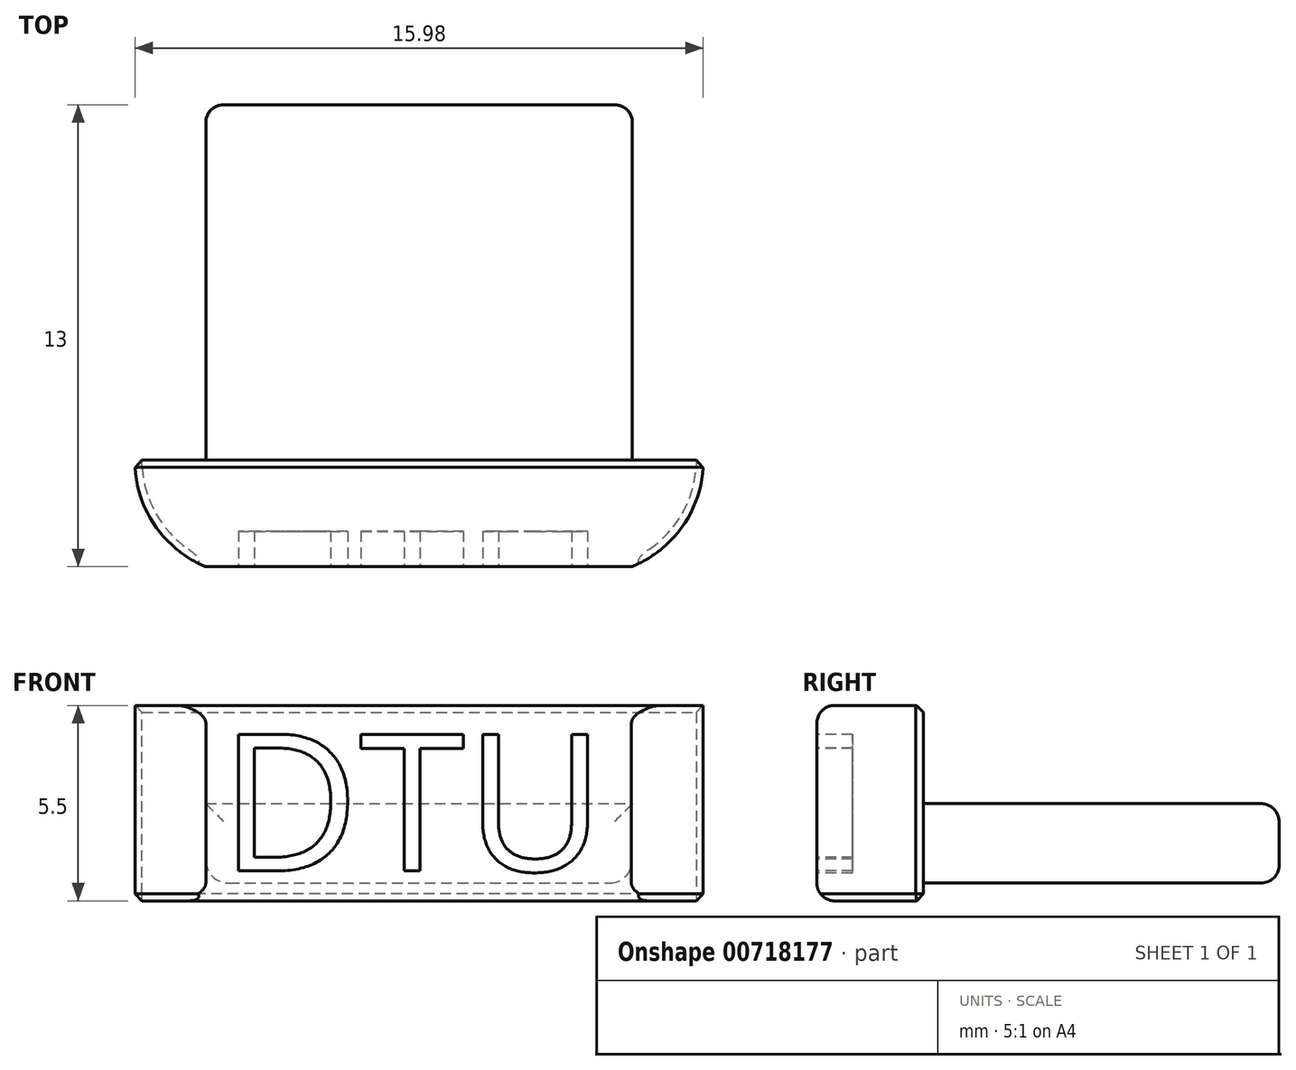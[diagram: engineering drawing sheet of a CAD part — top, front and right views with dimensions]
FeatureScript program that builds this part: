
annotation { "Feature Type Name" : "Feature", "Feature Type Description" : "" }
export const myFeature = defineFeature(function(context is Context, id is Id, definition is map)
    precondition{}
    {
        {
            var Q0;
            Q0=qCreatedBy(makeId("Front.planeOp"),FACE);
            var sketch = newSketch(context, id + "F0", { "sketchPlane" : qUnion([Q0])});
            skLineSegment(sketch, "E0.bottom", {"start": v(0.64, 0) * mm, "end": v(11.36, 0) * mm});
            skLineSegment(sketch, "E1.top", {"start": v(0.31, 2.24) * mm, "end": v(11.69, 2.24) * mm});
            skPoint(sketch, "E2.visualSharp", {"position": v(12, 4.5) * mm});
            skPoint(sketch, "E3.visualSharp", {"position": v(0, 4.5) * mm});
            skPoint(sketch, "E4.visualSharp", {"position": v(0, 0) * mm});
            skArc(sketch, "E4.filletArc", {"start": v(0, 0.64) * mm, "mid": v(0.19, 0.19) * mm, "end": v(0.64, 0) * mm});
            skPoint(sketch, "E5.visualSharp", {"position": v(12, 0) * mm});
            skArc(sketch, "E5.filletArc", {"start": v(11.36, 0) * mm, "mid": v(11.81, 0.19) * mm, "end": v(12, 0.64) * mm});
            skPoint(sketch, "E6.visualSharp", {"position": v(0.31, 4.18) * mm});
            skPoint(sketch, "E7.visualSharp", {"position": v(11.69, 4.18) * mm});
            skPoint(sketch, "E8.visualSharp", {"position": v(0.32, 0.31) * mm});
            skPoint(sketch, "E9.visualSharp", {"position": v(11.69, 0.32) * mm});
            skLineSegment(sketch, "E10", {"start": v(0.31, 2.24) * mm, "end": v(0, 2.24) * mm});
            skLineSegment(sketch, "E11", {"start": v(11.69, 2.24) * mm, "end": v(12, 2.24) * mm});
            skLineSegment(sketch, "E12", {"start": v(12, 0.64) * mm, "end": v(12, 2.24) * mm});
            skLineSegment(sketch, "E13", {"start": v(0, 0.64) * mm, "end": v(0, 2.24) * mm});
            skSolve(sketch);
        }
        {
            var Q0;
            Q0=makeQuery(id+"F0.imprint","IMPRINT",FACE,{"disambiguationData":[TD([[makeQuery(id+"F0.imprint","IMPRINT",EDGE,{"derivedFrom":sQuery(id+"F0.wireOp",EDGE,"E0.bottom")}),1.0]])]});
            var Q1;
            Q1=makeQuery(id+"F0.imprint","IMPRINT",FACE,{"disambiguationData":[TD([[makeQuery(id+"F0.imprint","IMPRINT",EDGE,{"derivedFrom":sQuery(id+"F0.wireOp",EDGE,"E1.bottom")}),-1.0]])]});
            extrude(context, id + "F1", {"entities" : qUnion([Q0, Q1]), "depth" : 10 * mm, "offsetDistance" : 25 * mm});
        }
        {
            var Q0;
            Q0=makeQuery(id+"F1.opExtrude","CAP_FACE",FACE,{"disambiguationData":[OSD([sQuery(id+"F0.wireOp",EDGE,"E0.bottom"),sQuery(id+"F0.wireOp",EDGE,"E0.top"),sQuery(id+"F0.wireOp",EDGE,"E0.left"),sQuery(id+"F0.wireOp",EDGE,"E0.right"),sQuery(id+"F0.wireOp",EDGE,"E2.filletArc"),sQuery(id+"F0.wireOp",EDGE,"E3.filletArc"),sQuery(id+"F0.wireOp",EDGE,"E4.filletArc"),sQuery(id+"F0.wireOp",EDGE,"E5.filletArc")])],"isStart":false});
            var sketch = newSketch(context, id + "F2", { "sketchPlane" : qUnion([Q0])});
            skLineSegment(sketch, "E14.bottom", {"start": v(-2, 5) * mm, "end": v(14, 5) * mm});
            skLineSegment(sketch, "E14.top", {"start": v(-2, -0.5) * mm, "end": v(14, -0.5) * mm});
            skLineSegment(sketch, "E14.left", {"start": v(-2, 5) * mm, "end": v(-2, -0.5) * mm});
            skLineSegment(sketch, "E14.right", {"start": v(14, 5) * mm, "end": v(14, -0.5) * mm});
            skPoint(sketch, "E15.visualSharp", {"position": v(-2, 5) * mm});
            skLineSegment(sketch, "E15.filletArc", {"start": v(-2, 5) * mm, "end": v(-2, 5) * mm});
            skPoint(sketch, "E16.visualSharp", {"position": v(14, 5) * mm});
            skLineSegment(sketch, "E16.filletArc", {"start": v(14, 5) * mm, "end": v(14, 5) * mm});
            skPoint(sketch, "E17.visualSharp", {"position": v(14, -0.5) * mm});
            skLineSegment(sketch, "E17.filletArc", {"start": v(14, -0.5) * mm, "end": v(14, -0.5) * mm});
            skPoint(sketch, "E18.visualSharp", {"position": v(-2, -0.5) * mm});
            skLineSegment(sketch, "E18.filletArc", {"start": v(-2, -0.5) * mm, "end": v(-2, -0.5) * mm});
            skSolve(sketch);
        }
        {
            var Q0;
            Q0=makeQuery(id+"F2.imprint","IMPRINT",FACE,{"disambiguationData":[TD([[makeQuery(id+"F2.imprint","IMPRINT",EDGE,{"derivedFrom":sQuery(id+"F2.wireOp",EDGE,"E14.bottom")}),-1.0]])]});
            var Q1;
            Q1=makeQuery(id+"F2.imprint","IMPRINT",FACE,{"disambiguationData":[TD([[makeQuery(id+"F2.imprint","IMPRINT",EDGE,{"derivedFrom":makeQuery(id+"F1.opExtrude","CAP_EDGE",EDGE,{"disambiguationData":[OSD([sQuery(id+"F0.wireOp",EDGE,"E0.bottom")])],"isStart":false})}),1.0]])]});
            extrude(context, id + "F3", {"entities" : qUnion([Q0, Q1]), "operationType" : NewBodyOperationType.ADD, "depth" : 3 * mm, "offsetDistance" : 25 * mm});
        }
        {
            var Q0;
            Q0=makeQuery(id+"F3.opExtrude","SWEPT_FACE",FACE,{"disambiguationData":[OSD([sQuery(id+"F2.wireOp",EDGE,"E14.bottom")])]});
            var sketch = newSketch(context, id + "F4", { "sketchPlane" : qUnion([Q0])});
            skArc(sketch, "E19", {"start": v(-2, -10) * mm, "mid": v(-1.45, -11.8) * mm, "end": v(0, -13) * mm});
            skArc(sketch, "E20", {"start": v(11.97, -13) * mm, "mid": v(13.45, -11.81) * mm, "end": v(14, -10) * mm});
            skSolve(sketch);
        }
        {
            var Q0;
            {var subQ1=sQuery(id+"F2.wireOp",EDGE,"E14.bottom");var subQ2=makeQuery(id+"F3.opExtrude","SWEPT_EDGE",EDGE,{"disambiguationData":[OSD([subQ1,sQuery(id+"F2.wireOp",EDGE,"E14.right")])]});Q0=makeQuery(id+"F4.imprint","IMPRINT",FACE,{"disambiguationData":[TD([[makeQuery(id+"F4.imprint","IMPRINT",EDGE,{"derivedFrom":subQ2}),1.0]])]});}
            var Q1;
            {var subQ0=sQuery(id+"F4.wireOp",EDGE,"E19");Q1=makeQuery(id+"F4.imprint","IMPRINT",FACE,{"disambiguationData":[TD([[makeQuery(id+"F4.imprint","IMPRINT",EDGE,{"derivedFrom":subQ0}),-1.0]])]});}
            extrude(context, id + "F5", {"entities" : qUnion([Q0, Q1]), "operationType" : NewBodyOperationType.REMOVE, "oppositeDirection" : true, "depth" : 10 * mm, "offsetDistance" : 25 * mm});
        }
        {
            var Q0;
            Q0=makeQuery(id+"F3.opExtrude","CAP_EDGE",EDGE,{"disambiguationData":[OSD([sQuery(id+"F2.wireOp",EDGE,"E14.bottom")])],"isStart":true});
            var Q1;
            {var subQ0=sQuery(id+"F2.wireOp",EDGE,"E14.right");Q1=makeQuery(id+"F5.boolean.opBoolean","MERGE",EDGE,{"derivedFrom":[makeQuery(id+"F3.opExtrude","CAP_EDGE",EDGE,{"disambiguationData":[OSD([subQ0])],"isStart":true})],"fromTools":[makeQuery(id+"F5.opExtrude","SWEPT_EDGE",EDGE,{"disambiguationData":[OSD([sQuery(id+"F2.wireOp",EDGE,"E14.bottom"),subQ0,sQuery(id+"F4.wireOp",EDGE,"E20")])]})]});}
            var Q2;
            Q2=makeQuery(id+"F3.opExtrude","CAP_EDGE",EDGE,{"disambiguationData":[OSD([sQuery(id+"F2.wireOp",EDGE,"E14.top")])],"isStart":true});
            var Q3;
            {var subQ0=sQuery(id+"F2.wireOp",EDGE,"E14.left");Q3=makeQuery(id+"F5.boolean.opBoolean","MERGE",EDGE,{"derivedFrom":[makeQuery(id+"F3.opExtrude","CAP_EDGE",EDGE,{"disambiguationData":[OSD([subQ0])],"isStart":true})],"fromTools":[makeQuery(id+"F5.opExtrude","SWEPT_EDGE",EDGE,{"disambiguationData":[OSD([sQuery(id+"F2.wireOp",EDGE,"E14.bottom"),subQ0,sQuery(id+"F4.wireOp",EDGE,"E19")])]})]});}
            var Q4;
            Q4=makeQuery(id+"F5.boolean.opBoolean","COPY",EDGE,{"derivedFrom":makeQuery(id+"F5.opExtrude","CAP_EDGE",EDGE,{"disambiguationData":[OSD([sQuery(id+"F4.wireOp",EDGE,"E19")])],"isStart":true})});
            var Q5;
            Q5=makeQuery(id+"F5.boolean.opBoolean","COPY",EDGE,{"derivedFrom":makeQuery(id+"F5.opExtrude","CAP_EDGE",EDGE,{"disambiguationData":[OSD([sQuery(id+"F4.wireOp",EDGE,"E20")])],"isStart":true})});
            var Q6;
            Q6=makeQuery(id+"F5.boolean.opBoolean","INTERSECT",EDGE,{"derivedFrom":[makeQuery(id+"F3.opExtrude","SWEPT_FACE",FACE,{"disambiguationData":[OSD([sQuery(id+"F2.wireOp",EDGE,"E14.top")])]}),makeQuery(id+"F5.opExtrude","SWEPT_FACE",FACE,{"disambiguationData":[OSD([sQuery(id+"F4.wireOp",EDGE,"E19")])]})]});
            var Q7;
            Q7=makeQuery(id+"F5.boolean.opBoolean","INTERSECT",EDGE,{"derivedFrom":[makeQuery(id+"F3.opExtrude","SWEPT_FACE",FACE,{"disambiguationData":[OSD([sQuery(id+"F2.wireOp",EDGE,"E14.top")])]}),makeQuery(id+"F5.opExtrude","SWEPT_FACE",FACE,{"disambiguationData":[OSD([sQuery(id+"F4.wireOp",EDGE,"E20")])]})]});
            chamfer(context, id + "F6", {"entities" : qUnion([Q0, Q1, Q2, Q3, Q4, Q5, Q6, Q7]), "width" : 0.2 * mm, "tangentPropagation" : true});
        }
        {
            var Q0;
            Q0=makeQuery(id+"F3.opExtrude","CAP_FACE",FACE,{"disambiguationData":[OSD([sQuery(id+"F2.wireOp",EDGE,"E14.bottom"),sQuery(id+"F2.wireOp",EDGE,"E14.top"),sQuery(id+"F2.wireOp",EDGE,"E14.left"),sQuery(id+"F2.wireOp",EDGE,"E14.right")])],"isStart":false});
            var sketch = newSketch(context, id + "F7", { "sketchPlane" : qUnion([Q0])});
            skText(sketch, "E21", { "text": "DTU", "fontName": "OpenSans-Regular.ttf"});
            const initialGuessF7  = {"E21": [0.00039, 0.00034, 1, 0, 0.00388]};
            skSetInitialGuess(sketch, initialGuessF7);
            skSolve(sketch);
        }
        {
            var Q0;
            Q0 = qSketchRegion(id + "F7", true);
            extrude(context, id + "F8", {"entities" : qUnion([Q0]), "operationType" : NewBodyOperationType.REMOVE, "oppositeDirection" : true, "depth" : 1 * mm, "offsetDistance" : 25 * mm});
        }
        {
            var Q0;
            Q0=makeQuery(id+"F1.opExtrude","CAP_EDGE",EDGE,{"disambiguationData":[OSD([sQuery(id+"F0.wireOp",EDGE,"E0.bottom")])],"isStart":true});
            var Q1;
            Q1=makeQuery(id+"F1.opExtrude","CAP_EDGE",EDGE,{"disambiguationData":[OSD([sQuery(id+"F0.wireOp",EDGE,"E1.top"),sQuery(id+"F0.wireOp",EDGE,"E10"),sQuery(id+"F0.wireOp",EDGE,"E11")])],"isStart":true});
            var Q2;
            Q2=makeQuery(id+"F3.opExtrude","CAP_EDGE",EDGE,{"disambiguationData":[OSD([sQuery(id+"F2.wireOp",EDGE,"E14.bottom")])],"isStart":false});
            var Q3;
            Q3=makeQuery(id+"F3.opExtrude","CAP_EDGE",EDGE,{"disambiguationData":[OSD([sQuery(id+"F2.wireOp",EDGE,"E14.top")])],"isStart":false});
            fillet(context, id + "F9", {"entities" : qUnion([Q0, Q1, Q2, Q3]), "tangentPropagation" : true, "radius" : 0.5 * mm, "defaultsChanged" : false, "vertexSettings" : [], "allowEdgeOverflow" : false});
        }
    });
